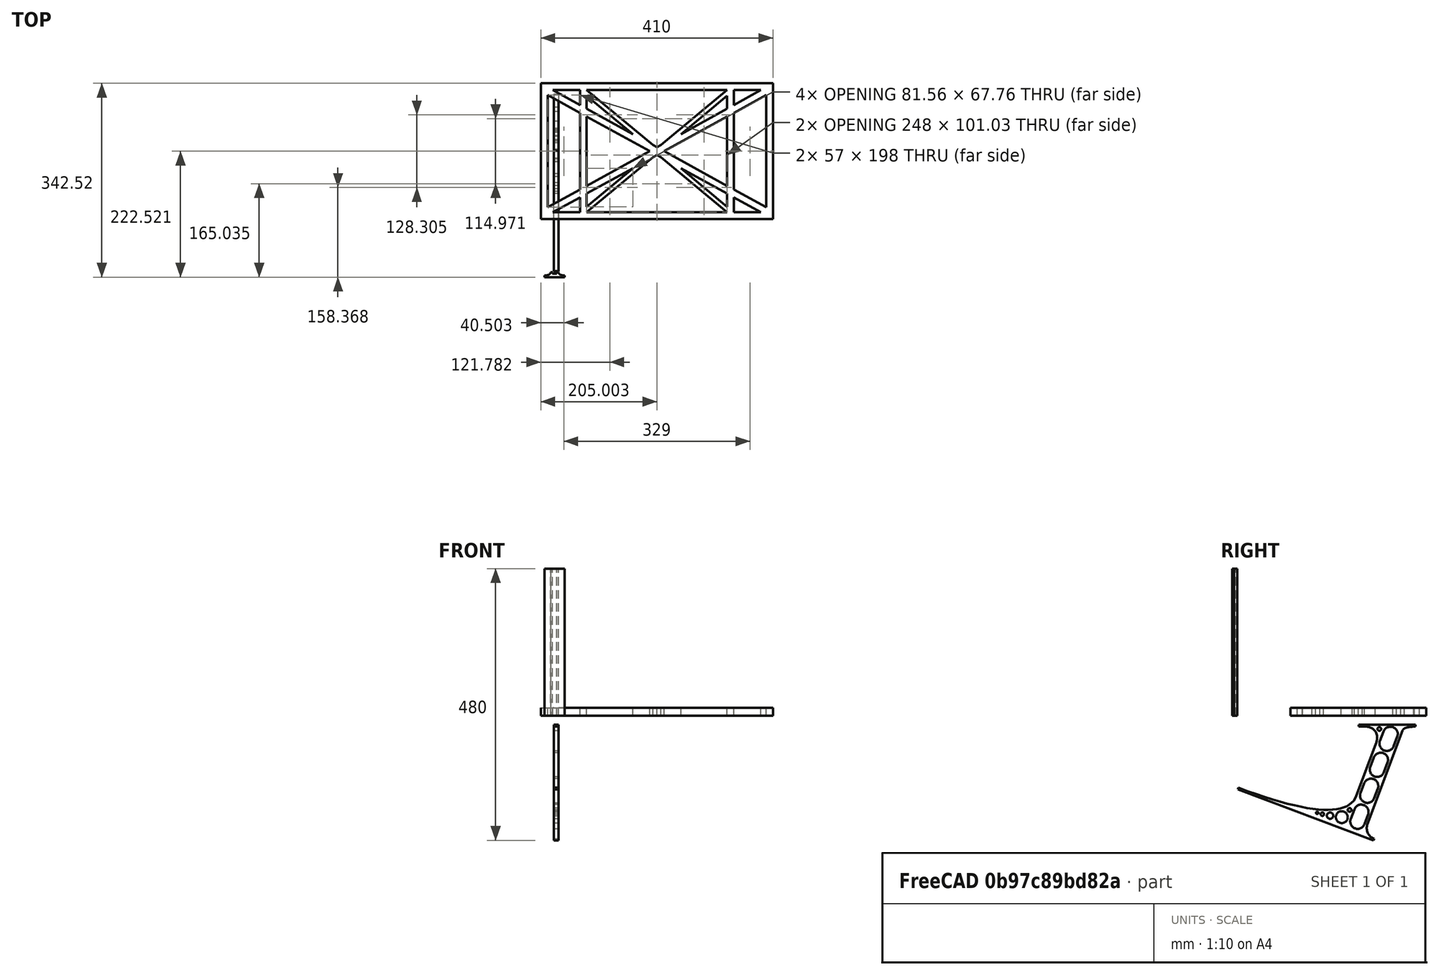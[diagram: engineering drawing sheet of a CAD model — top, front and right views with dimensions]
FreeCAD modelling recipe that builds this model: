
FCSTD DOCUMENT  (FreeCAD 0.19R0.19.2)
Label: laptopStand042
License: All rights reserved
LicenseURL: http://en.wikipedia.org/wiki/All_rights_reserved
objects: Sketcher::SketchObject×3, Part::Extrusion×3
note: 6 computed .brp shape members not serialized (recipe doc carries the construction recipe); baked Part::Feature solids carry a one-line shape summary decoded from their .brp

FEATURE [Sketcher::SketchObject] Sketch
  FullyConstrained = false
  sketch-geometry (58):
    g0: LineSegment StartX=-22.9272 StartY=136.221 StartZ=0 EndX=387.073 EndY=136.221 EndZ=0
    g1: LineSegment StartX=-22.9272 StartY=-103.779 StartZ=0 EndX=387.073 EndY=-103.779 EndZ=0
    g2: LineSegment StartX=375.073 StartY=115.221 StartZ=0 EndX=318.073 EndY=83.9235 EndZ=0
    g3: LineSegment StartX=-10.9272 StartY=-82.7794 StartZ=0 EndX=46.0728 EndY=-51.4823 EndZ=0
    g4: LineSegment StartX=-1.92719 StartY=124.221 StartZ=0 EndX=46.0728 EndY=97.8651 EndZ=0
    g5: LineSegment StartX=366.073 StartY=-91.7794 StartZ=0 EndX=318.073 EndY=-65.424 EndZ=0
    g6: LineSegment StartX=-10.9272 StartY=115.221 StartZ=0 EndX=-10.9272 EndY=-82.7794 EndZ=0
    g7: LineSegment StartX=375.073 StartY=-82.7794 StartZ=0 EndX=375.073 EndY=115.221 EndZ=0
    g8: LineSegment StartX=-1.92719 StartY=-91.7794 StartZ=0 EndX=46.0728 EndY=-91.7794 EndZ=0
    g9: LineSegment StartX=318.073 StartY=124.221 StartZ=0 EndX=366.073 EndY=124.221 EndZ=0
    g10: LineSegment StartX=306.073 StartY=-81.8102 StartZ=0 EndX=224.513 EndY=-14.0532 EndZ=0
    g11: LineSegment StartX=58.0728 StartY=114.251 StartZ=0 EndX=139.632 EndY=46.4944 EndZ=0
    g12: LineSegment StartX=306.073 StartY=124.221 StartZ=0 EndX=189.124 EndY=27.0628 EndZ=0
    g13: LineSegment StartX=58.0728 StartY=-91.7794 StartZ=0 EndX=175.022 EndY=5.37834 EndZ=0
    g14: LineSegment StartX=46.0728 StartY=124.221 StartZ=0 EndX=46.0728 EndY=97.8651 EndZ=0
    g15: LineSegment StartX=58.0728 StartY=-81.8102 StartZ=0 EndX=58.0728 EndY=-58.8351 EndZ=0
    g16: LineSegment StartX=318.073 StartY=124.221 StartZ=0 EndX=318.073 EndY=97.8651 EndZ=0
    g17: LineSegment StartX=306.073 StartY=114.251 StartZ=0 EndX=306.073 EndY=91.2763 EndZ=0
    g18: LineSegment StartX=182.073 StartY=23.1914 StartZ=0 EndX=189.124 EndY=27.0628 EndZ=0
    g19: LineSegment StartX=182.073 StartY=9.24976 StartZ=0 EndX=175.022 EndY=5.37834 EndZ=0
    g20: LineSegment StartX=224.513 StartY=46.4944 StartZ=0 EndX=306.073 EndY=114.251 EndZ=0
    g21: LineSegment StartX=175.022 StartY=27.0628 StartZ=0 EndX=58.0728 EndY=124.221 EndZ=0
    g22: LineSegment StartX=169.377 StartY=16.2206 StartZ=0 EndX=58.0728 EndY=77.3346 EndZ=0
    g23: LineSegment StartX=139.632 StartY=-14.0532 StartZ=0 EndX=58.0728 EndY=-81.8102 EndZ=0
    g24: LineSegment StartX=194.768 StartY=16.2206 StartZ=0 EndX=306.073 EndY=-44.8935 EndZ=0
    g25: LineSegment StartX=224.513 StartY=46.4944 StartZ=0 EndX=306.073 EndY=91.2763 EndZ=0
    g26: LineSegment StartX=175.022 StartY=27.0628 StartZ=0 EndX=182.073 EndY=23.1914 EndZ=0
    g27: LineSegment StartX=139.632 StartY=-14.0532 StartZ=0 EndX=58.0728 EndY=-58.8351 EndZ=0
    g28: LineSegment StartX=189.124 StartY=5.37834 StartZ=0 EndX=182.073 EndY=9.24976 EndZ=0
    g29: LineSegment StartX=189.124 StartY=5.37834 StartZ=0 EndX=306.073 EndY=-91.7794 EndZ=0
    g30: LineSegment StartX=306.073 StartY=77.3346 StartZ=0 EndX=306.073 EndY=-44.8935 EndZ=0
    g31: LineSegment StartX=318.073 StartY=83.9235 StartZ=0 EndX=318.073 EndY=-51.4823 EndZ=0
    g32: LineSegment StartX=318.073 StartY=97.8651 StartZ=0 EndX=366.073 EndY=124.221 EndZ=0
    g33: LineSegment StartX=306.073 StartY=77.3346 StartZ=0 EndX=194.768 EndY=16.2206 EndZ=0
    g34: LineSegment StartX=306.073 StartY=-58.8351 StartZ=0 EndX=224.513 EndY=-14.0532 EndZ=0
    g35: LineSegment StartX=306.073 StartY=-58.8351 StartZ=0 EndX=306.073 EndY=-81.8102 EndZ=0
    g36: LineSegment StartX=318.073 StartY=-51.4823 StartZ=0 EndX=375.073 EndY=-82.7794 EndZ=0
    g37: LineSegment StartX=318.073 StartY=-65.424 StartZ=0 EndX=318.073 EndY=-91.7794 EndZ=0
    g38: LineSegment StartX=306.073 StartY=124.221 StartZ=0 EndX=58.0728 EndY=124.221 EndZ=0
    g39: LineSegment StartX=318.073 StartY=-91.7794 StartZ=0 EndX=366.073 EndY=-91.7794 EndZ=0
    g40: LineSegment StartX=58.0728 StartY=-91.7794 StartZ=0 EndX=306.073 EndY=-91.7794 EndZ=0
    g41: LineSegment StartX=58.0728 StartY=-44.8935 StartZ=0 EndX=58.0728 EndY=77.3346 EndZ=0
    g42: LineSegment StartX=46.0728 StartY=-65.424 StartZ=0 EndX=-1.92719 EndY=-91.7794 EndZ=0
    g43: LineSegment StartX=46.0728 StartY=-65.424 StartZ=0 EndX=46.0728 EndY=-91.7794 EndZ=0
    g44: LineSegment StartX=58.0728 StartY=-44.8935 StartZ=0 EndX=169.377 EndY=16.2206 EndZ=0
    g45: LineSegment StartX=58.0728 StartY=91.2763 StartZ=0 EndX=58.0728 EndY=114.251 EndZ=0
    g46: LineSegment StartX=46.0728 StartY=83.9235 StartZ=0 EndX=46.0728 EndY=-51.4823 EndZ=0
    g47: LineSegment StartX=46.0728 StartY=124.221 StartZ=0 EndX=-1.92719 EndY=124.221 EndZ=0
    g48: LineSegment StartX=58.0728 StartY=91.2763 StartZ=0 EndX=139.632 EndY=46.4944 EndZ=0
    g49: LineSegment StartX=46.0728 StartY=83.9235 StartZ=0 EndX=-10.9272 EndY=115.221 EndZ=0
    g50: LineSegment StartX=-22.9272 StartY=136.221 StartZ=0 EndX=-42.9272 EndY=136.221 EndZ=0
    g51: LineSegment StartX=387.073 StartY=136.221 StartZ=0 EndX=407.073 EndY=136.221 EndZ=0
    g52: LineSegment StartX=-42.9272 StartY=136.221 StartZ=0 EndX=-42.9272 EndY=-103.779 EndZ=0
    g53: LineSegment StartX=-22.9272 StartY=-103.779 StartZ=0 EndX=-42.9272 EndY=-103.779 EndZ=0
    g54: LineSegment StartX=407.073 StartY=136.221 StartZ=0 EndX=407.073 EndY=-103.779 EndZ=0
    g55: LineSegment StartX=387.073 StartY=-103.779 StartZ=0 EndX=407.073 EndY=-103.779 EndZ=0
    g56: LineSegment StartX=175.022 StartY=27.0628 StartZ=0 EndX=175.022 EndY=129.202 EndZ=0
    g57: LineSegment StartX=189.124 StartY=27.0628 StartZ=0 EndX=188.404 EndY=127.984 EndZ=0
  constraints (115):
    c: Horizontal(g0)
    c: Distance(g0) = 410
    c: Horizontal(g1)
    c: Block(g0)
    c: Horizontal(g8)
    c: Horizontal(g9)
    c: PointOnObject(g33,g4)
    c: Coincident(g26,g18)
    c: Coincident(g28,g19)
    c: Tangent(g5,g22)
    c: PointOnObject(g22,g3)
    c: PointOnObject(g24,g2)
    c: Coincident(g18,g12)
    c: Tangent(g18,g25)
    c: Coincident(g48,g11)
    c: Coincident(g26,g21)
    c: Coincident(g20,g25)
    c: Coincident(g19,g13)
    c: Coincident(g27,g23)
    c: Tangent(g19,g27)
    c: Coincident(g34,g10)
    c: Coincident(g29,g28)
    c: Coincident(g20,g17)
    c: Tangent(g17,g30)
    c: Tangent(g16,g31)
    c: Coincident(g25,g17)
    c: Tangent(g25,g32)
    c: Coincident(g2,g31)
    c: Coincident(g33,g30)
    c: Tangent(g2,g33)
    c: Coincident(g35,g10)
    c: Tangent(g5,g34)
    c: Tangent(g30,g35)
    c: Coincident(g24,g30)
    c: Tangent(g24,g36)
    c: Coincident(g31,g36)
    c: Coincident(g37,g5)
    c: Tangent(g31,g37)
    c: Coincident(g23,g15)
    c: Tangent(g15,g41)
    c: Coincident(g27,g15)
    c: Tangent(g27,g42)
    c: Coincident(g43,g42)
    c: Tangent(g14,g43)
    c: Coincident(g3,g46)
    c: Coincident(g44,g41)
    c: Tangent(g3,g44)
    c: Tangent(g41,g45)
    c: Tangent(g14,g46)
    c: Coincident(g11,g45)
    c: PointOnObject(g38,g21)
    c: Tangent(g38,g47)
    c: Coincident(g4,g14)
    c: Coincident(g48,g45)
    c: Tangent(g4,g48)
    c: Coincident(g22,g41)
    c: Coincident(g49,g46)
    c: Tangent(g22,g49)
    c: Block(g21)
    c: Block(g12)
    c: Block(g18)
    c: Block(g38)
    c: Block(g16)
    c: Block(g32)
    c: Block(g2)
    c: Block(g36)
    c: Block(g7)
    c: Block(g34)
    c: Block(g35)
    c: Block(g5)
    c: Block(g37)
    c: Block(g20)
    c: Block(g29)
    c: Block(g40)
    c: Block(g19)
    c: Block(g13)
    c: Block(g27)
    c: Block(g23)
    c: Block(g43)
    c: Block(g42)
    c: Block(g3)
    c: Block(g6)
    c: Block(g49)
    c: Block(g4)
    c: Block(g14)
    c: Block(g11)
    c: Block(g45)
    c: Block(g33)
    c: Block(g30)
    c: Block(g22)
    c: Block(g44)
    c: Block(g47)
    c: Block(g9)
    c: Block(g39)
    c: Block(g8)
    c: Horizontal(g50)
    c: Distance(g50) = 20
    c: Coincident(g51,g0)
    c: Horizontal(g51)
    c: Distance(g51) = 20
    c: Coincident(g52,g50)
    c: Vertical(g52)
    c: Horizontal(g53)
    c: Coincident(g53,g52)
    c: Coincident(g54,g51)
    c: Vertical(g54)
    c: Coincident(g55,g1)
    c: Horizontal(g55)
    c: Coincident(g55,g54)
    c: Block(g54)
    c: Block(g53)
    c: Block(g52)
    c: Block(g1)
    c: Coincident(g56,g21)
    c: Vertical(g56)
FEATURE [Sketcher::SketchObject] Sketch001
  FullyConstrained = true
  MapMode = 4
  Placement = pos=(0,0,0) rot=(0.57735,0.57735,0.57735;2.0944rad)
  Support = -> [Sketch]
  sketch-geometry (46):
    g0: BSplineCurve PolesCount=3 KnotsCount=2 Degree=2 IsPeriodic=0
    g1: ArcOfCircle CenterX=73.122 CenterY=-32.2909 CenterZ=0 NormalX=0 NormalY=0 NormalZ=1 AngleXU=0 Radius=13 StartAngle=5.92268 EndAngle=9.06428
    g2: ArcOfCircle CenterX=66.7816 CenterY=-49.1439 CenterZ=0 NormalX=0 NormalY=0 NormalZ=1 AngleXU=0 Radius=13 StartAngle=2.78068 EndAngle=5.92131
    g3: ArcOfCircle CenterX=55.9263 CenterY=-78.1807 CenterZ=0 NormalX=0 NormalY=0 NormalZ=1 AngleXU=0 Radius=13 StartAngle=5.92268 EndAngle=9.06428
    g4: ArcOfCircle CenterX=49.5884 CenterY=-95.0342 CenterZ=0 NormalX=0 NormalY=0 NormalZ=1 AngleXU=0 Radius=13 StartAngle=2.78068 EndAngle=5.92131
    g5: ArcOfCircle CenterX=38.7206 CenterY=-124.067 CenterZ=0 NormalX=0 NormalY=0 NormalZ=1 AngleXU=0 Radius=13 StartAngle=5.92268 EndAngle=9.06428
    g6: ArcOfCircle CenterX=32.3875 CenterY=-140.92 CenterZ=0 NormalX=0 NormalY=0 NormalZ=1 AngleXU=0 Radius=13 StartAngle=2.78068 EndAngle=5.92131
    g7: ArcOfCircle CenterX=21.4715 CenterY=-169.934 CenterZ=0 NormalX=0 NormalY=0 NormalZ=1 AngleXU=0 Radius=13 StartAngle=5.92268 EndAngle=9.06428
    g8: ArcOfCircle CenterX=15.1336 CenterY=-186.787 CenterZ=0 NormalX=0 NormalY=0 NormalZ=1 AngleXU=0 Radius=13 StartAngle=2.78068 EndAngle=5.92131
    g9-g12: Circle x4 (B-spline internal-alignment scaffolding for g13; pole/knot coordinates omitted)
    g13: BSplineCurve PolesCount=4 KnotsCount=2 Degree=3 IsPeriodic=0
    g14: GeomPoint X=28.8094 Y=-19.0875 Z=0
    g15: GeomPoint X=47.0443 Y=-50.4712 Z=0
    g16: Circle CenterX=53.5586 CenterY=-23.2695 CenterZ=0 NormalX=0 NormalY=0 NormalZ=1 AngleXU=0 Radius=3.24518
    g17: Circle CenterX=-195.441 CenterY=-127.082 CenterZ=0 NormalX=0 NormalY=0 NormalZ=1 AngleXU=0 Radius=1
    g18: Circle CenterX=-8.24091 CenterY=-197.481 CenterZ=0 NormalX=0 NormalY=0 NormalZ=1 AngleXU=0 Radius=1
    g19: Circle CenterX=12.8789 CenterY=-141.321 CenterZ=0 NormalX=0 NormalY=0 NormalZ=1 AngleXU=0 Radius=1
    g20: BSplineCurve PolesCount=3 KnotsCount=2 Degree=2 IsPeriodic=0
    g21: GeomPoint X=-195.441 Y=-127.082 Z=0
    g22: GeomPoint X=12.8789 Y=-141.321 Z=0
    g23: Circle CenterX=-12.8016 CenterY=-179.036 CenterZ=0 NormalX=0 NormalY=0 NormalZ=1 AngleXU=0 Radius=10.5072
    g24: Circle CenterX=0.933922 CenterY=-166.43 CenterZ=0 NormalX=0 NormalY=0 NormalZ=1 AngleXU=0 Radius=3.26661
    g25: Circle CenterX=-33.5518 CenterY=-176.44 CenterZ=0 NormalX=0 NormalY=0 NormalZ=1 AngleXU=0 Radius=5.64388
    g26: Circle CenterX=-47.2366 CenterY=-173.859 CenterZ=0 NormalX=0 NormalY=0 NormalZ=1 AngleXU=0 Radius=3.01653
    g27: Circle CenterX=-56.2595 CenterY=-171.456 CenterZ=0 NormalX=0 NormalY=0 NormalZ=1 AngleXU=0 Radius=2.12826
    g28: ArcOfCircle CenterX=51.2151 CenterY=-198.473 CenterZ=0 NormalX=0 NormalY=0 NormalZ=1 AngleXU=0 Radius=20 StartAngle=2.78189 EndAngle=4.35269
    g29: LineSegment StartX=32.4951 StartY=-191.433 StartZ=0 EndX=94.6577 EndY=-26.1351 EndZ=0
    g30: LineSegment StartX=43.1192 StartY=-220.001 StartZ=0 EndX=-196.497 EndY=-129.89 EndZ=0
    g31: LineSegment StartX=43.1192 StartY=-220.001 StartZ=0 EndX=44.1752 EndY=-217.193 EndZ=0
    g32: LineSegment StartX=117.223 StartY=-19.0875 StartZ=0 EndX=117.223 EndY=-16.0875 EndZ=0
    g33: LineSegment StartX=117.223 StartY=-16.0875 StartZ=0 EndX=17.2232 EndY=-16.0875 EndZ=0
    g34: LineSegment StartX=17.2232 StartY=-16.0875 StartZ=0 EndX=17.2232 EndY=-19.0875 EndZ=0
    g35: LineSegment StartX=28.8094 StartY=-19.0875 StartZ=0 EndX=17.2232 EndY=-19.0875 EndZ=0
    g36: LineSegment StartX=47.0443 StartY=-50.4712 StartZ=0 EndX=12.8789 EndY=-141.321 EndZ=0
    g37: LineSegment StartX=-195.441 StartY=-127.082 StartZ=0 EndX=-196.497 EndY=-129.89 EndZ=0
    g38: LineSegment StartX=85.2864 StartY=-36.8765 StartZ=0 EndX=78.9396 EndY=-53.7463 EndZ=0
    g39: LineSegment StartX=60.9577 StartY=-27.7052 StartZ=0 EndX=54.6191 EndY=-44.5532 EndZ=0
    g40: LineSegment StartX=68.0907 StartY=-82.7664 StartZ=0 EndX=61.7465 EndY=-99.6365 EndZ=0
    g41: LineSegment StartX=43.7619 StartY=-73.595 StartZ=0 EndX=37.426 EndY=-90.4435 EndZ=0
    g42: LineSegment StartX=50.885 StartY=-128.652 StartZ=0 EndX=44.5456 EndY=-145.522 EndZ=0
    g43: LineSegment StartX=26.5562 StartY=-119.481 StartZ=0 EndX=20.2251 EndY=-136.329 EndZ=0
    g44: LineSegment StartX=9.3071 StartY=-165.349 StartZ=0 EndX=2.97115 EndY=-182.197 EndZ=0
    g45: LineSegment StartX=33.6358 StartY=-174.52 StartZ=0 EndX=27.2917 EndY=-191.39 EndZ=0
  constraints (70):
    c: Block(g0)
    c: Block(g1)
    c: Block(g2)
    c: Block(g4)
    c: Block(g3)
    c: Block(g6)
    c: Block(g5)
    c: Block(g8)
    c: Block(g7)
    c: Weight(g9) = 1
    c: Equal(g9,g10)
    c: Equal(g9,g11)
    c: Equal(g9,g12)
    c: InternalAlignment(g9-g12 -> g13) x4
    c: InternalAlignment(g14,g13)
    c: InternalAlignment(g15,g13)
    c: Block(g16)
    c: Weight(g17) = 1
    c: Equal(g17,g18)
    c: Equal(g17,g19)
    c: InternalAlignment(g17,g20)
    c: InternalAlignment(g18,g20)
    c: InternalAlignment(g19,g20)
    c: InternalAlignment(g21,g20)
    c: InternalAlignment(g22,g20)
    c: Block(g20)
    c: Block(g23)
    c: Block(g24)
    c: Block(g25)
    c: Block(g26)
    c: Block(g27)
    c: Block(g28)
    c: Coincident(g29,g28)
    c: Coincident(g29,g0)
    c: Block(g13)
    c: Coincident(g31,g30)
    c: Coincident(g31,g28)
    c: Block(g31)
    c: Coincident(g32,g0)
    c: Vertical(g32)
    c: Coincident(g33,g32)
    c: Horizontal(g33)
    c: Coincident(g34,g33)
    c: Vertical(g34)
    c: Block(g33)
    c: Coincident(g35,g13)
    c: Coincident(g35,g34)
    c: Horizontal(g35)
    c: Coincident(g36,g13)
    c: Coincident(g36,g20)
    c: Coincident(g37,g20)
    c: Coincident(g37,g30)
    c: Block(g30)
    c: Coincident(g38,g1)
    c: Coincident(g38,g2)
    c: Coincident(g39,g1)
    c: Coincident(g39,g2)
    c: Coincident(g40,g3)
    c: Coincident(g40,g4)
    c: Coincident(g41,g3)
    c: Coincident(g41,g4)
    c: Coincident(g42,g5)
    c: Coincident(g42,g6)
    c: Coincident(g43,g5)
    c: Coincident(g43,g6)
    c: Coincident(g44,g7)
    c: Coincident(g44,g8)
    c: Coincident(g45,g7)
    c: Coincident(g45,g8)
    c: Distance(g30) = 256
FEATURE [Part::Extrusion] Extrude002
  Base = -> Sketch001
  Dir = (1,0,0)
  DirMode = 2
  FaceMakerClass = Part::FaceMakerBullseye
  LengthFwd = 8
  LengthRev = 0
  Solid = true
  Symmetric = false
FEATURE [Sketcher::SketchObject] Sketch002
  FullyConstrained = true
  sketch-geometry (20):
    g0: LineSegment StartX=-2.77179 StartY=-200.304 StartZ=0 EndX=5.22821 EndY=-200.304 EndZ=0
    g1: LineSegment StartX=5.22821 StartY=-200.304 StartZ=0 EndX=5.22821 EndY=-197.304 EndZ=0
    g2: LineSegment StartX=-2.77179 StartY=-200.304 StartZ=0 EndX=-2.77179 EndY=-197.304 EndZ=0
    g3: LineSegment StartX=5.22821 StartY=-197.304 StartZ=0 EndX=8.22821 EndY=-197.304 EndZ=0
    g4: LineSegment StartX=-2.77179 StartY=-197.304 StartZ=0 EndX=-5.77179 EndY=-197.304 EndZ=0
    g5: LineSegment StartX=19.2282 StartY=-203.304 StartZ=0 EndX=19.2282 EndY=-206.304 EndZ=0
    g6: LineSegment StartX=-16.7718 StartY=-203.304 StartZ=0 EndX=-16.7718 EndY=-206.304 EndZ=0
    g7: LineSegment StartX=-16.7718 StartY=-206.304 StartZ=0 EndX=19.2282 EndY=-206.304 EndZ=0
    g8: Circle CenterX=-16.7718 CenterY=-203.304 CenterZ=0 NormalX=0 NormalY=0 NormalZ=1 AngleXU=0 Radius=1
    g9: Circle CenterX=-5.77179 CenterY=-203.304 CenterZ=0 NormalX=0 NormalY=0 NormalZ=1 AngleXU=0 Radius=1
    g10: Circle CenterX=-5.77179 CenterY=-197.304 CenterZ=0 NormalX=0 NormalY=0 NormalZ=1 AngleXU=0 Radius=1
    g11: BSplineCurve PolesCount=3 KnotsCount=2 Degree=2 IsPeriodic=0
    g12: GeomPoint X=-16.7718 Y=-203.304 Z=0
    g13: GeomPoint X=-5.77179 Y=-197.304 Z=0
    g14: Circle CenterX=19.2282 CenterY=-203.304 CenterZ=0 NormalX=0 NormalY=0 NormalZ=1 AngleXU=0 Radius=1
    g15: Circle CenterX=8.22821 CenterY=-203.304 CenterZ=0 NormalX=0 NormalY=0 NormalZ=1 AngleXU=0 Radius=1
    g16: Circle CenterX=8.22821 CenterY=-197.304 CenterZ=0 NormalX=0 NormalY=0 NormalZ=1 AngleXU=0 Radius=1
    g17: BSplineCurve PolesCount=3 KnotsCount=2 Degree=2 IsPeriodic=0
    g18: GeomPoint X=19.2282 Y=-203.304 Z=0
    g19: GeomPoint X=8.22821 Y=-197.304 Z=0
  constraints (41):
    c: Horizontal(g0)
    c: Distance(g0) = 8
    c: Coincident(g1,g0)
    c: Vertical(g1)
    c: Distance(g1) = 3
    c: Coincident(g2,g0)
    c: Vertical(g2)
    c: Distance(g2) = 3
    c: Coincident(g3,g1)
    c: Horizontal(g3)
    c: Distance(g3) = 3
    c: Coincident(g4,g2)
    c: Horizontal(g4)
    c: Distance(g4) = 3
    c: Vertical(g5)
    c: Vertical(g6)
    c: Coincident(g7,g6)
    c: Coincident(g7,g5)
    c: Weight(g8) = 1
    c: Equal(g8,g9)
    c: Equal(g8,g10)
    c: Coincident(g11,g4)
    c: InternalAlignment(g8,g11)
    c: InternalAlignment(g9,g11)
    c: InternalAlignment(g10,g11)
    c: InternalAlignment(g12,g11)
    c: InternalAlignment(g13,g11)
    c: Coincident(g17,g5)
    c: Weight(g14) = 1
    c: Equal(g14,g15)
    c: Equal(g14,g16)
    c: Coincident(g17,g3)
    c: InternalAlignment(g14,g17)
    c: InternalAlignment(g15,g17)
    c: InternalAlignment(g16,g17)
    c: InternalAlignment(g18,g17)
    c: InternalAlignment(g19,g17)
    c: Block(g7)
    c: Block(g17)
    c: Block(g11)
    c: Block(g6)
FEATURE [Part::Extrusion] Extrude003
  Base = -> Sketch002
  Dir = (0,0,1)
  DirMode = 2
  FaceMakerClass = Part::FaceMakerBullseye
  LengthFwd = 260
  LengthRev = 0
  Solid = true
  Symmetric = false
FEATURE [Part::Extrusion] Extrude
  Base = -> Sketch
  Dir = (0,0,1)
  DirMode = 2
  FaceMakerClass = Part::FaceMakerBullseye
  LengthFwd = 14
  LengthRev = 0
  Solid = true
  Symmetric = false
